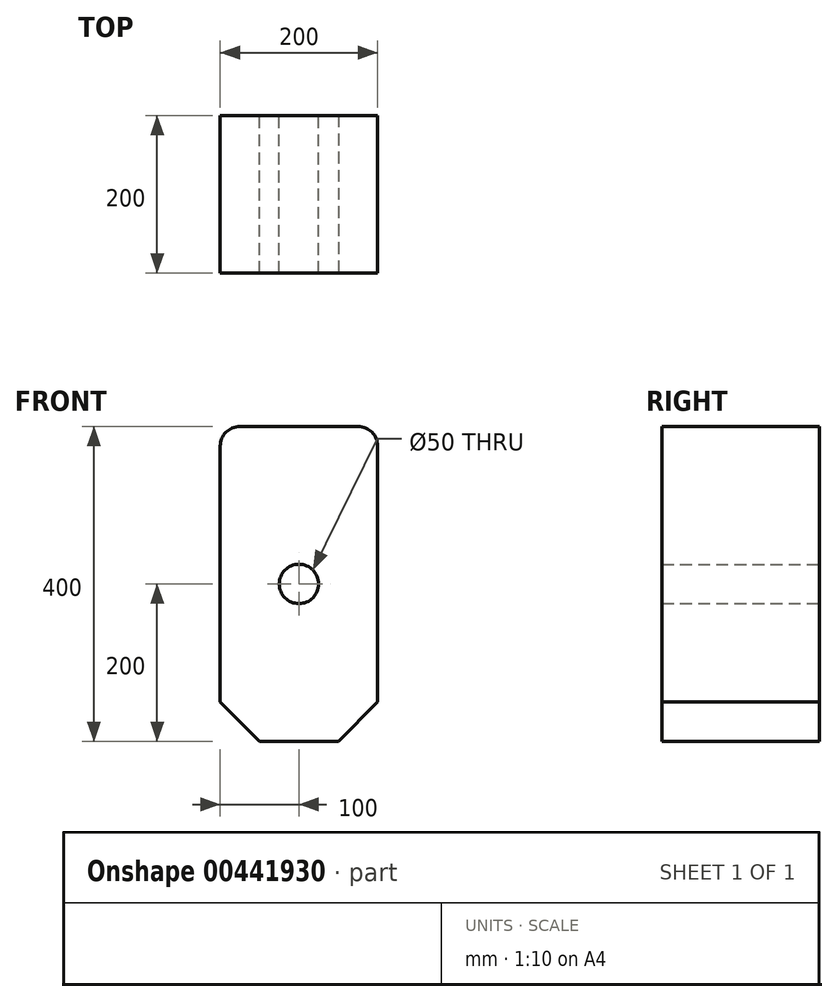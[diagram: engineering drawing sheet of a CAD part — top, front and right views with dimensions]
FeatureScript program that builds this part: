
annotation { "Feature Type Name" : "Feature", "Feature Type Description" : "" }
export const myFeature = defineFeature(function(context is Context, id is Id, definition is map)
    precondition{}
    {
        {
            var Q0;
            Q0=qCreatedBy(makeId("Front.planeOp"),FACE);
            var sketch = newSketch(context, id + "F0", { "sketchPlane" : qUnion([Q0])});
            skLineSegment(sketch, "E0.bottom", {"start": v(75, 200) * mm, "end": v(-75, 200) * mm});
            skLineSegment(sketch, "E0.top", {"start": v(100, -200) * mm, "end": v(-100, -200) * mm});
            skLineSegment(sketch, "E0.left", {"start": v(100, 175) * mm, "end": v(100, -200) * mm});
            skLineSegment(sketch, "E0.right", {"start": v(-100, 175) * mm, "end": v(-100, -200) * mm});
            skPoint(sketch, "E0.middle", {"position": v(0, 0) * mm});
            skPoint(sketch, "E1.visualSharp", {"position": v(-100, 200) * mm});
            skArc(sketch, "E1.filletArc", {"start": v(-75, 200) * mm, "mid": v(-92.68, 192.68) * mm, "end": v(-100, 175) * mm});
            skPoint(sketch, "E2.visualSharp", {"position": v(100, 200) * mm});
            skArc(sketch, "E2.filletArc", {"start": v(100, 175) * mm, "mid": v(92.68, 192.68) * mm, "end": v(75, 200) * mm});
            skCircle(sketch, "E3", {"center": v(0, 0) * mm, "radius": 25 * mm});
            skSolve(sketch);
        }
        {
            var Q0;
            Q0 = qSketchRegion(id + "F0", true);
            extrude(context, id + "F1", {"entities" : qUnion([Q0]), "depth" : 200 * mm});
        }
        {
            var Q0;
            Q0=makeQuery(id+"F1.opExtrude","SWEPT_EDGE",EDGE,{"disambiguationData":[OSD([sQuery(id+"F0.wireOp",EDGE,"E0.top"),sQuery(id+"F0.wireOp",EDGE,"E0.right")])]});
            var Q1;
            Q1=makeQuery(id+"F1.opExtrude","SWEPT_EDGE",EDGE,{"disambiguationData":[OSD([sQuery(id+"F0.wireOp",EDGE,"E0.top"),sQuery(id+"F0.wireOp",EDGE,"E0.left")])]});
            chamfer(context, id + "F2", {"entities" : qUnion([Q0, Q1]), "width" : 50 * mm, "tangentPropagation" : true});
        }
    });
